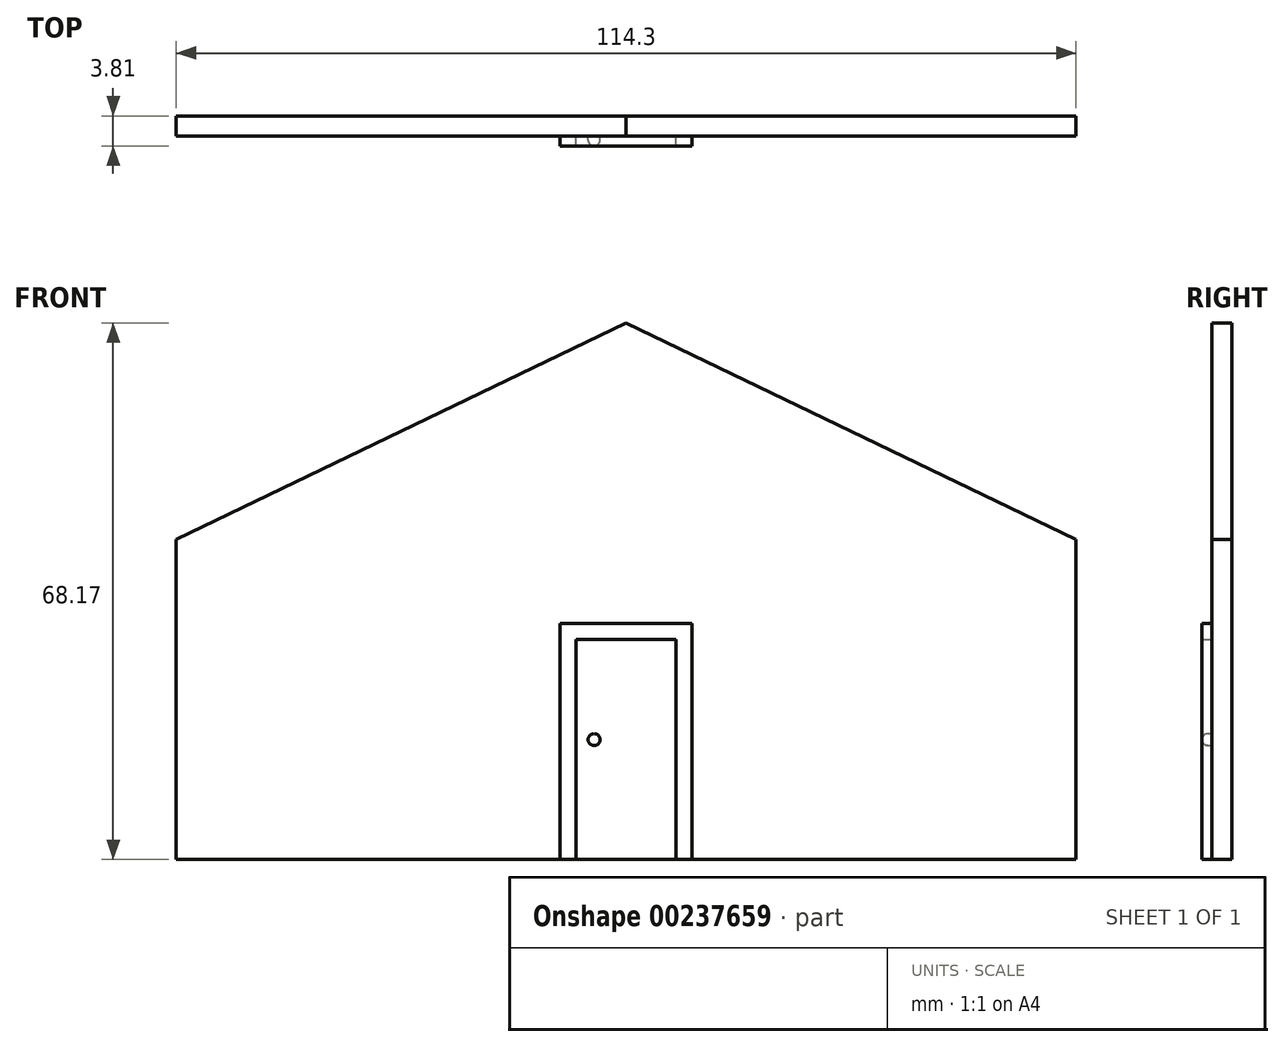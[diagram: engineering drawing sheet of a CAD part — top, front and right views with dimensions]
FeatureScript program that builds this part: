
annotation { "Feature Type Name" : "Feature", "Feature Type Description" : "" }
export const myFeature = defineFeature(function(context is Context, id is Id, definition is map)
    precondition{}
    {
        {
            var Q0;
            Q0=qCreatedBy(makeId("Front.planeOp"),FACE);
            var sketch = newSketch(context, id + "F0", { "sketchPlane" : qUnion([Q0])});
            skLineSegment(sketch, "E0.bottom", {"start": v(-6.35, 13.97) * mm, "end": v(6.35, 13.97) * mm});
            skLineSegment(sketch, "E0.top", {"start": v(-6.35, -13.97) * mm, "end": v(6.35, -13.97) * mm});
            skLineSegment(sketch, "E0.left", {"start": v(-6.35, 13.97) * mm, "end": v(-6.35, -13.97) * mm});
            skLineSegment(sketch, "E0.right", {"start": v(6.35, 13.97) * mm, "end": v(6.35, -13.97) * mm});
            skPoint(sketch, "E0.middle", {"position": v(0, 0) * mm});
            skLineSegment(sketch, "E1.bottom", {"start": v(-57.15, -13.97) * mm, "end": v(57.15, -13.97) * mm});
            skLineSegment(sketch, "E1.top", {"start": v(-57.15, 26.67) * mm, "end": v(57.15, 26.67) * mm});
            skLineSegment(sketch, "E1.left", {"start": v(-57.15, -13.97) * mm, "end": v(-57.15, 26.67) * mm});
            skLineSegment(sketch, "E1.right", {"start": v(57.15, -13.97) * mm, "end": v(57.15, 26.67) * mm});
            skLineSegment(sketch, "E2", {"start": v(0, 54.2) * mm, "end": v(-57.15, 26.67) * mm});
            skPoint(sketch, "E2.startSnap0", {"position": v(0, 26.67) * mm});
            skLineSegment(sketch, "E3", {"start": v(0, 54.2) * mm, "end": v(57.15, 26.67) * mm});
            skLineSegment(sketch, "E4.bottom", {"start": v(-8.38, -13.97) * mm, "end": v(8.38, -13.97) * mm});
            skLineSegment(sketch, "E4.top", {"start": v(-8.38, 16) * mm, "end": v(8.38, 16) * mm});
            skLineSegment(sketch, "E4.left", {"start": v(-8.38, -13.97) * mm, "end": v(-8.38, 16) * mm});
            skLineSegment(sketch, "E4.right", {"start": v(8.38, -13.97) * mm, "end": v(8.38, 16) * mm});
            skCircle(sketch, "E5", {"center": v(-4.06, 1.27) * mm, "radius": 0.76 * mm});
            skLineSegment(sketch, "E6.direction2", {"start": v(-57.15, -9.5) * mm, "end": v(-57.15, -5.59) * mm, "construction": true});
            skSolve(sketch);
        }
        {
            var Q0;
            Q0=makeQuery(id+"F0.imprint","IMPRINT",FACE,{"disambiguationData":[TD([[makeQuery(id+"F0.imprint","IMPRINT",EDGE,{"derivedFrom":sQuery(id+"F0.wireOp",EDGE,"E1.top")}),1.0]])]});
            var Q1;
            Q1=makeQuery(id+"F0.imprint","IMPRINT",FACE,{"disambiguationData":[TD([[makeQuery(id+"F0.imprint","IMPRINT",EDGE,{"derivedFrom":sQuery(id+"F0.wireOp",EDGE,"E1.top")}),-1.0]])]});
            var Q2;
            Q2=makeQuery(id+"F0.imprint","IMPRINT",FACE,{"disambiguationData":[TD([[makeQuery(id+"F0.imprint","IMPRINT",EDGE,{"derivedFrom":sQuery(id+"F0.wireOp",EDGE,"E0.bottom")}),-1.0]])]});
            extrude(context, id + "F1", {"entities" : qUnion([Q0, Q1, Q2]), "depth" : 2.54 * mm});
        }
        {
            var Q0;
            Q0=makeQuery(id+"F0.imprint","IMPRINT",FACE,{"disambiguationData":[TD([[makeQuery(id+"F0.imprint","IMPRINT",EDGE,{"derivedFrom":sQuery(id+"F0.wireOp",EDGE,"JhyOcFHf-lFlv-rtJ0-EV2h-klalowO8GC4o.bottom")}),-1.0]])]});
            var Q1;
            Q1=makeQuery(id+"F0.imprint","IMPRINT",FACE,{"disambiguationData":[TD([[makeQuery(id+"F0.imprint","IMPRINT",EDGE,{"derivedFrom":sQuery(id+"F0.wireOp",EDGE,"ee944c5a-e7ab-43e9-a902-48614a2fd3250.MirrorCS")}),-1.0]])]});
            var Q2;
            Q2=makeQuery(id+"F0.imprint","IMPRINT",FACE,{"disambiguationData":[TD([[makeQuery(id+"F0.imprint","IMPRINT",EDGE,{"derivedFrom":sQuery(id+"F0.wireOp",EDGE,"E0.bottom")}),1.0]])]});
            extrude(context, id + "F2", {"entities" : qUnion([Q0, Q1, Q2]), "operationType" : NewBodyOperationType.ADD, "depth" : 3.8 * mm});
        }
        {
            var Q0;
            Q0=makeQuery(id+"F0.imprint","IMPRINT",FACE,{"disambiguationData":[TD([[makeQuery(id+"F0.imprint","IMPRINT",EDGE,{"derivedFrom":sQuery(id+"F0.wireOp",EDGE,"E5")}),1.0]])]});
            extrude(context, id + "F3", {"entities" : qUnion([Q0]), "operationType" : NewBodyOperationType.ADD, "depth" : 3.8 * mm});
        }
        {
            var Q0;
            Q0=makeQuery(id+"F3.opExtrude","CAP_EDGE",EDGE,{"disambiguationData":[OSD([sQuery(id+"F0.wireOp",EDGE,"E5")])],"isStart":false});
            fillet(context, id + "F4", {"entities" : qUnion([Q0]), "radius" : 0.76 * mm, "tangentPropagation" : true, "allowEdgeOverflow" : false});
        }
    });
